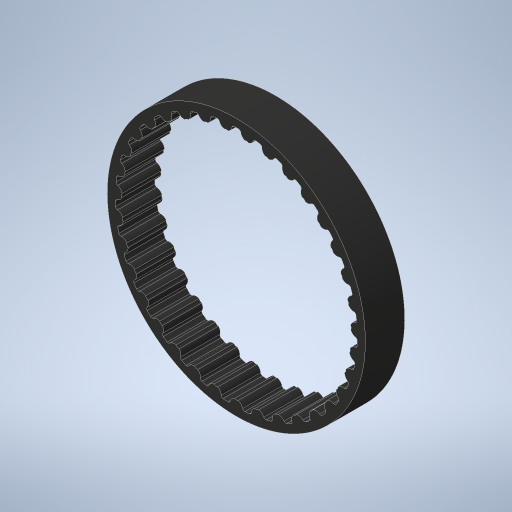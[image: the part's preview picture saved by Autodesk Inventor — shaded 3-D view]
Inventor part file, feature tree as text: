
AUTODESK INVENTOR PART (.ipt)
format: ipt  version: 2023.3 (Build 273359000, 359)  size: 805,888 bytes
history: native  units: in
note: dims shown in document units (in); Inventor stores cm internally (conversion verified against a paired STEP export)
features: extrude x3, sketch x3, projected_geometry x3, plane x1, other x1, pattern_circular x1
ambient origin geometry x8: Origin, YZ Plane, XZ Plane, XY Plane, X Axis, Y Axis, Z Axis, Center Point
bodies: Solid1 (feature_tree)
feature tree (12):
  extrude  "Extrusion1"  Depth=0.0197in
  plane  "Work Plane1"
  sketch  "Sketch2"  dims[d3=0.0591in]
  other  "Work Axis1"
  pattern_circular  "Circular Pattern1"  [2 undecoded]
  sketch  "Sketch3"  dims[d4=0.0328in d5=0.0591in d6=0.0197in d7=0.0748in d8=0.0945in d9=0.0762in d10=0.0762in d11=0.0655in d12=0.0197in d13=0.0748in d14=0.0in d15=0.25in d16=0.0191in d17=0.0408in d18=0.0148in d19=0.042in d20=0.3543in d21=0.0in d23=13.7795in d24=360.0deg d26=2.3246in d27=0.125in d28=0.0in d29=0.0in d30=1.0in d31=0.0in]
  extrude  "Extrusion2"  Depth=0.0197in
  extrude  "Extrusion3"  Depth=0.3543in
  sketch  "Sketch1"  dims[d1=0.0444in d2=0.0197in]
  projected_geometry  "Projected Loop1"
  projected_geometry  "Project Cut Edges1"
  projected_geometry  "Project Cut Edges2"
note: 2 required parameter values undecoded (feature->parameter linkage not recoverable at this tier; creation-order binding heuristic only, values carry confidence <= 0.55)
